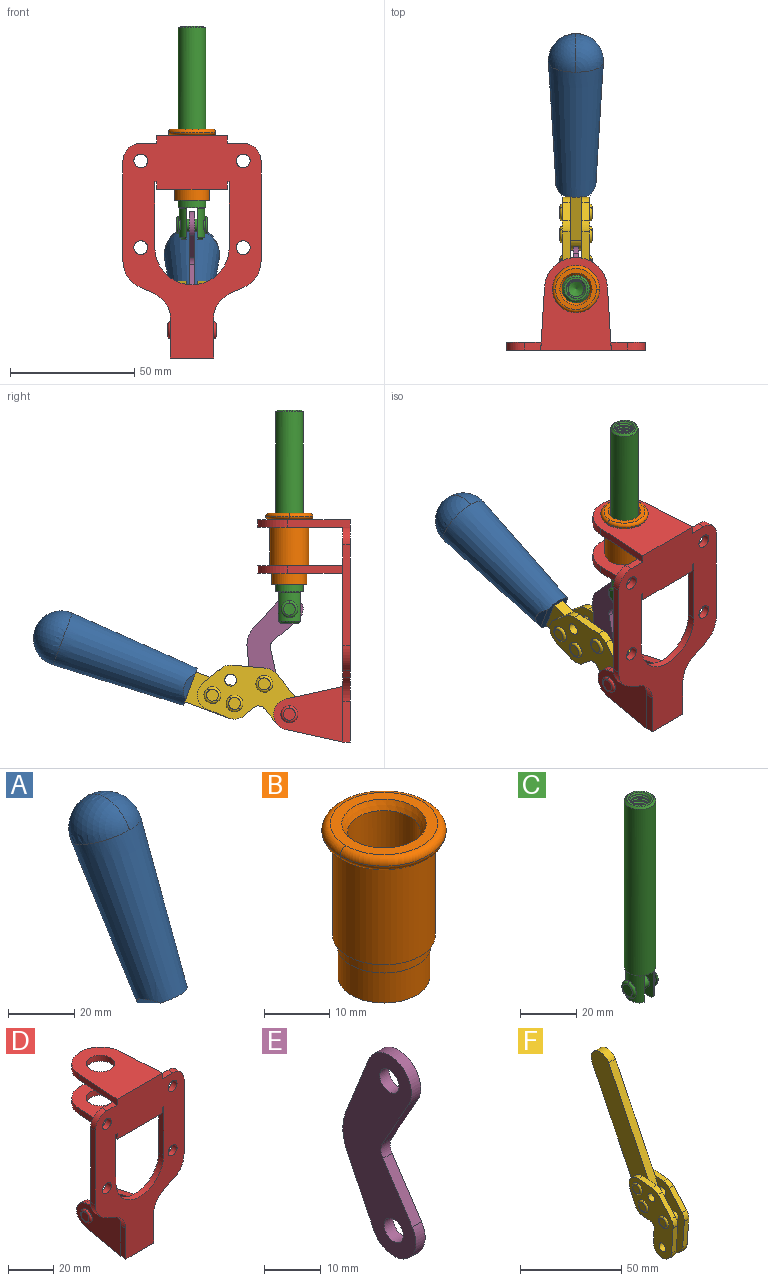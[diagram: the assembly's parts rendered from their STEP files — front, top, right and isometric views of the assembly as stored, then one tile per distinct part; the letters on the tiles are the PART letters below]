
ASSEMBLY  parts=6 mates=6
PART A: 11 faces, bbox 22.3x42.6x64.5 mm
  f0: sphere r=11.13mm, area 411.4mm2, adj f1,f8
  f1: cone r=11.11mm half-angle=3.3deg, axis (0,0.44,0.9), area 3251.8mm2, adj f0,f7,f8,f9,f10
  f2: cylinder r=6.16mm len=11.7mm, axis (1,0,0), area 89.5mm2, adj f3,f4,f5,f6
  f3: plane 60.23x36.75mm, normal (-1,0,0), area 763.6mm2, adj f2,f4,f6,f10
  f4: plane 51.37x25.05mm, normal (0,0.9,-0.44), area 264.2mm2, adj f2,f3,f5,f10
  f5: plane 60.23x36.75mm, normal (1,0,0), area 763.6mm2, adj f2,f4,f6,f10
  f6: plane 51.37x25.05mm, normal (0,-0.9,0.44), area 264.2mm2, adj f2,f3,f5,f10
  f7: plane 9.95x5.95mm, normal (0.71,-0.31,-0.64), area 25.8mm2, adj f1,f10
  f8: sphere r=11.13mm, area 411.4mm2, adj f0,f1
  f9: plane 9.95x5.95mm, normal (-0.71,-0.31,-0.64), area 25.8mm2, adj f1,f10
  f10: plane 14.27x11.38mm, normal (0,-0.44,-0.9), area 106.7mm2, adj f1,f3,f4,f5,f6,f7,f9
PART B: 15 faces, bbox 20.6x20.6x28.7 mm
  f0: torus R=8.26mm, axis (0,0,1), area 56.8mm2, adj f1,f10,f12
  f1: torus R=8.26mm, axis (0,0,1), area 56.8mm2, adj f0,f6,f13
  f2: cylinder r=5.59mm len=25.91mm, axis (0,0,1), area 909.6mm2, adj f3,f4
  f3: cone r=6.86mm half-angle=45deg, axis (0,0,-1), area 70.2mm2, adj f2,f14
  f4: cone r=6.47mm half-angle=30deg, axis (0,0,1), area 66.7mm2, adj f2,f13
  f5: cylinder r=7.04mm len=14.07mm, axis (0,0,1), area 252.6mm2, adj f11,f14
  f6: torus R=8.26mm, axis (0,0,1), area 56.8mm2, adj f1,f12,f13
  f7: cylinder r=7.16mm len=14.33mm, axis (0,0,1), area 91.5mm2, adj f9,f11
  f8: cylinder r=7.86mm len=18.42mm, axis (0,0,1), area 909.6mm2, adj f9,f10
  f9: plane 15.72x15.72mm, normal (0,0,-1), area 33mm2, adj f7,f8
  f10: plane 16.51x16.51mm, normal (0,0,-1), area 19.9mm2, adj f0,f8,f12
  f11: plane 14.33x14.33mm, normal (0,0,-1), area 5.7mm2, adj f5,f7
  f12: torus R=8.26mm, axis (0,0,1), area 56.8mm2, adj f0,f6,f10
  f13: plane 16.51x16.51mm, normal (0,0,1), area 82.7mm2, adj f1,f4,f6
  f14: plane 14.07x14.07mm, normal (0,0,-1), area 7.8mm2, adj f3,f5
PART C: 48 faces, bbox 12.6x11.1x86.1 mm
  f0: torus R=2.41mm, axis (-1,0,0), area 15mm2, adj f30,f32,f34
  f1: torus R=2.41mm, axis (-1,0,0), area 15mm2, adj f29,f31,f33
  f2: cylinder r=5.54mm len=72.39mm, axis (0,0,1), area 2518.5mm2, adj f3,f4,f42,f43
  f3: cone r=5.54mm half-angle=45deg, axis (0,0,1), area 7.6mm2, adj f2,f5,f41
  f4: cone r=5.54mm half-angle=45deg, axis (0,0,-1), area 34.9mm2, adj f2,f39
  f5: cylinder r=5.08mm len=11.48mm, axis (0,0,1), area 108.3mm2, adj f3,f7,f8,f41
  f6: cylinder r=2.41mm len=4.83mm, axis (-1,0,0), area 71.2mm2, adj f40,f41
  f7: cylinder r=2.41mm len=4.83mm, axis (-1,0,0), area 7.6mm2, adj f5,f34
  f8: cone r=5.08mm half-angle=45deg, axis (0,0,1), area 10.6mm2, adj f5,f37,f41
  f9: cone r=3.98mm half-angle=45deg, axis (0,0,1), area 17.6mm2, adj f27,f39,f45,f46,f47
  f10: cylinder r=2.41mm len=4.83mm, axis (-1,0,0), area 7.6mm2, adj f33,f38
  f11: cylinder r=3.2mm len=6.4mm, axis (0,0,1), area 78.4mm2, adj f12,f28,f44,f45,f47
  f12: cylinder r=3.2mm len=6.4mm, axis (0,0,1), area 10.5mm2, adj f11,f13,f45,f47
  f13: cylinder r=3.2mm len=6.4mm, axis (0,0,1), area 10.5mm2, adj f12,f14,f45,f47
  f14: cylinder r=3.2mm len=6.4mm, axis (0,0,1), area 10.5mm2, adj f13,f15,f45,f47
  f15: cylinder r=3.2mm len=6.4mm, axis (0,0,1), area 10.5mm2, adj f14,f16,f45,f47
  f16: cylinder r=3.2mm len=6.4mm, axis (0,0,1), area 10.5mm2, adj f15,f17,f45,f47
  f17: cylinder r=3.2mm len=6.4mm, axis (0,0,1), area 10.5mm2, adj f16,f18,f45,f47
  f18: cylinder r=3.2mm len=6.4mm, axis (0,0,1), area 10.5mm2, adj f17,f19,f45,f47
  f19: cylinder r=3.2mm len=6.4mm, axis (0,0,1), area 10.5mm2, adj f18,f20,f45,f47
  f20: cylinder r=3.2mm len=6.4mm, axis (0,0,1), area 10.5mm2, adj f19,f21,f45,f47
  f21: cylinder r=3.2mm len=6.4mm, axis (0,0,1), area 10.5mm2, adj f20,f22,f45,f47
  f22: cylinder r=3.2mm len=6.4mm, axis (0,0,1), area 10.5mm2, adj f21,f23,f45,f47
  f23: cylinder r=3.2mm len=6.4mm, axis (0,0,1), area 10.5mm2, adj f22,f24,f45,f47
  f24: cylinder r=3.2mm len=6.4mm, axis (0,0,1), area 10.5mm2, adj f23,f25,f45,f47
  f25: cylinder r=3.2mm len=6.4mm, axis (0,0,1), area 10.5mm2, adj f24,f26,f45,f47
  f26: cylinder r=3.2mm len=6.4mm, axis (0,0,1), area 10.5mm2, adj f25,f27,f45,f47
  f27: cylinder r=3.2mm len=6.4mm, axis (0,0,1), area 7.4mm2, adj f9,f26,f45,f47
  f28: cone r=3.2mm half-angle=60deg, axis (0,0,1), area 37.2mm2, adj f11
  f29: plane 4.83x4.83mm, normal (-1,0,0), area 18.3mm2, adj f1,f31
  f30: plane 4.83x4.83mm, normal (1,0,0), area 18.3mm2, adj f0,f32
  f31: torus R=2.41mm, axis (-1,0,0), area 15mm2, adj f1,f29,f33
  f32: torus R=2.41mm, axis (-1,0,0), area 15mm2, adj f0,f30,f34
  f33: plane 6.83x6.83mm, normal (1,0,0), area 18.3mm2, adj f1,f10,f31
  f34: plane 6.83x6.83mm, normal (-1,0,0), area 18.3mm2, adj f0,f7,f32
  f35: cone r=5.08mm half-angle=45deg, axis (0,0,1), area 10.6mm2, adj f36,f38,f40
  f36: plane 7.25x1.97mm, normal (0,0,-1), area 10mm2, adj f35,f40
  f37: plane 7.25x1.97mm, normal (0,0,-1), area 10mm2, adj f8,f41
  f38: cylinder r=5.08mm len=11.48mm, axis (0,0,1), area 108.3mm2, adj f10,f35,f40,f42
  f39: plane 9.55x9.55mm, normal (0,0,1), area 22mm2, adj f4,f9
  f40: plane 12.76x10.09mm, normal (1,0,0), area 95.7mm2, adj f6,f35,f36,f38,f42,f43
  f41: plane 12.76x10.09mm, normal (-1,0,0), area 95.7mm2, adj f3,f5,f6,f8,f37,f43
  f42: cone r=5.54mm half-angle=45deg, axis (0,0,1), area 7.6mm2, adj f2,f38,f40
  f43: plane 11.07x4.7mm, normal (0,0,-1), area 50.4mm2, adj f2,f40,f41
  f44: plane 0.89x0.62mm, normal (-1,0,0), area 0.3mm2, adj f11,f45,f46,f47
  f45: bspline ~24.8x7.63mm, area 266.6mm2, adj f9,f11,f12,f13,f14,f15,f16,f17
  f46: bspline ~24.87x7.63mm, area 73.6mm2, adj f9,f44,f45,f47
  f47: bspline ~24.98x7.63mm, area 272.5mm2, adj f9,f11,f12,f13,f14,f15,f16,f17
PART D: 55 faces, bbox 55.7x37.4x89.8 mm
  f0: torus R=2.41mm, axis (-1,0,0), area 15mm2, adj f11,f15,f25
  f1: torus R=2.41mm, axis (-1,0,0), area 15mm2, adj f10,f12,f22
  f2: cylinder r=2.78mm len=5.56mm, axis (0,-1,0), area 54.2mm2, adj f30,f54
  f3: cylinder r=14.99mm len=29.97mm, axis (0,-1,0), area 145.9mm2, adj f30,f49,f53,f54
  f4: cylinder r=2.78mm len=5.56mm, axis (0,-1,0), area 54.2mm2, adj f30,f54
  f5: cylinder r=2.78mm len=5.56mm, axis (0,-1,0), area 54.2mm2, adj f30,f54
  f6: cylinder r=2.78mm len=5.56mm, axis (0,-1,0), area 54.2mm2, adj f30,f54
  f7: cylinder r=6.35mm len=12.7mm, axis (0,0,1), area 123.6mm2, adj f27,f51
  f8: cylinder r=6.35mm len=12.7mm, axis (0,0,-1), area 124.7mm2, adj f21,f35
  f9: cylinder r=2.41mm len=11.18mm, axis (-1,0,0), area 169.4mm2, adj f16,f19
  f10: plane 4.83x4.83mm, normal (1,0,0), area 18.3mm2, adj f1,f12
  f11: plane 4.83x4.83mm, normal (-1,0,0), area 18.3mm2, adj f0,f15
  f12: torus R=2.41mm, axis (-1,0,0), area 15mm2, adj f1,f10,f22
  f13: cylinder r=6.35mm len=12.41mm, axis (1,0,0), area 53.4mm2, adj f18,f19,f22,f23
  f14: cylinder r=6.35mm len=12.41mm, axis (-1,0,0), area 53.4mm2, adj f16,f17,f24,f25
  f15: torus R=2.41mm, axis (-1,0,0), area 15mm2, adj f0,f11,f25
  f16: plane 27.86x22.35mm, normal (1,0,0), area 425.4mm2, adj f9,f14,f17,f24,f30
  f17: plane 22.86x4.97mm, normal (0,0.21,0.98), area 72.5mm2, adj f14,f16,f25,f30
  f18: plane 22.86x4.97mm, normal (0,0.21,0.98), area 72.5mm2, adj f13,f19,f22,f30
  f19: plane 27.86x22.35mm, normal (-1,0,0), area 425.4mm2, adj f9,f13,f18,f23,f30
  f20: cylinder r=12.7mm len=25.35mm, axis (0,0,-1), area 119.8mm2, adj f21,f34,f35,f36
  f21: plane 34.21x28.07mm, normal (0,0,-1), area 702.4mm2, adj f8,f20,f30,f34,f36
  f22: plane 27.96x22.45mm, normal (1,0,0), area 407.2mm2, adj f1,f12,f13,f18,f23,f30,f42,f43
  f23: plane 22.86x4.97mm, normal (0,0.21,-0.98), area 72.5mm2, adj f13,f19,f22,f44
  f24: plane 22.86x4.97mm, normal (0,0.21,-0.98), area 72.5mm2, adj f14,f16,f25,f44
  f25: plane 27.86x22.35mm, normal (-1,0,0), area 407.1mm2, adj f0,f14,f15,f17,f24,f30,f45,f46
  f26: plane 3.1x0.95mm, normal (0,0,-1), area 2.7mm2, adj f30,f49,f50,f54
  f27: plane 34.21x28.07mm, normal (0,0,1), area 702.4mm2, adj f7,f28,f30,f50,f52
  f28: cylinder r=12.7mm len=25.35mm, axis (0,0,1), area 118.8mm2, adj f27,f50,f51,f52
  f29: plane 3.1x0.95mm, normal (0,0,-1), area 2.7mm2, adj f30,f52,f53,f54
  f30: plane 86.54x55.63mm, normal (0,1,0), area 2362.9mm2, adj f2,f3,f4,f5,f6,f16,f17,f18
  f31: plane 40.56x3.1mm, normal (-1,0,0), area 125.7mm2, adj f30,f32,f48,f54
  f32: cylinder r=7.11mm len=7.11mm, axis (0,-1,0), area 34.6mm2, adj f30,f31,f33,f54
  f33: plane 6.67x3.1mm, normal (0,0,1), area 20.4mm2, adj f30,f32,f34,f54
  f34: plane 25.39x3.13mm, normal (-1,0.06,0), area 79.5mm2, adj f20,f21,f33,f35,f54
  f35: plane 37.31x28.45mm, normal (0,0,1), area 789.9mm2, adj f8,f20,f34,f36,f54
  f36: plane 25.39x3.13mm, normal (1,0.06,0), area 79.5mm2, adj f20,f21,f35,f37,f54
  f37: plane 6.67x3.1mm, normal (0,0,1), area 20.4mm2, adj f30,f36,f38,f54
  f38: cylinder r=7.11mm len=7.11mm, axis (0,-1,0), area 34.6mm2, adj f30,f37,f39,f54
  f39: plane 40.56x3.1mm, normal (1,0,0), area 125.7mm2, adj f30,f38,f40,f54
  f40: cylinder r=11.18mm len=10.16mm, axis (0,-1,0), area 39.5mm2, adj f30,f39,f41,f54
  f41: plane 6.09x3.1mm, normal (0.42,0,-0.91), area 20.8mm2, adj f30,f40,f42,f54
  f42: cylinder r=11.18mm len=9.41mm, axis (0,-1,0), area 37.2mm2, adj f22,f30,f41,f43,f54
  f43: plane 16.5x3.1mm, normal (1,0,0), area 51.1mm2, adj f22,f42,f44,f54
  f44: plane 17.37x3.1mm, normal (0,0,-1), area 53.8mm2, adj f23,f24,f30,f43,f45,f54
  f45: plane 16.5x3.1mm, normal (-1,0,0), area 51.1mm2, adj f25,f44,f46,f54
  f46: cylinder r=11.18mm len=9.41mm, axis (0,-1,0), area 37.2mm2, adj f25,f30,f45,f47,f54
  f47: plane 6.09x3.1mm, normal (-0.42,0,-0.91), area 20.8mm2, adj f30,f46,f48,f54
  f48: cylinder r=11.18mm len=10.16mm, axis (0,-1,0), area 39.5mm2, adj f30,f31,f47,f54
  f49: plane 26.54x3.1mm, normal (-1,0,0), area 82.3mm2, adj f3,f26,f30,f54
  f50: plane 25.39x3.1mm, normal (1,0.06,0), area 78.8mm2, adj f26,f27,f28,f51,f54
  f51: plane 37.31x28.45mm, normal (0,0,-1), area 789.9mm2, adj f7,f28,f50,f52,f54
  f52: plane 25.39x3.1mm, normal (-1,0.06,0), area 78.8mm2, adj f27,f28,f29,f51,f54
  f53: plane 26.54x3.1mm, normal (1,0,0), area 82.3mm2, adj f3,f29,f30,f54
  f54: plane 89.66x55.63mm, normal (0,-1,0), area 2678.5mm2, adj f2,f3,f4,f5,f6,f26,f29,f31
PART E: 12 faces, bbox 2.3x18.2x42.8 mm
  f0: cylinder r=2.4mm len=4.8mm, axis (1,0,0), area 34.9mm2, adj f4,f11
  f1: cylinder r=10.41mm len=8.47mm, axis (1,0,0), area 20.2mm2, adj f4,f9,f10,f11
  f2: cylinder r=3.05mm len=3.16mm, axis (1,0,0), area 7.7mm2, adj f4,f6,f7,f11
  f3: cylinder r=2.4mm len=4.8mm, axis (1,0,0), area 34.9mm2, adj f4,f11
  f4: plane 42.81x18.23mm, normal (-1,0,0), area 414.1mm2, adj f0,f1,f2,f3,f5,f6,f7,f8
  f5: cylinder r=5.54mm len=10.67mm, axis (1,0,0), area 41.8mm2, adj f4,f6,f10,f11
  f6: plane 11.66x6.53mm, normal (0,-0.87,-0.49), area 30.9mm2, adj f2,f4,f5,f11
  f7: plane 11.17x7.33mm, normal (0,-0.84,0.55), area 30.9mm2, adj f2,f4,f8,f11
  f8: cylinder r=5.54mm len=10.51mm, axis (1,0,0), area 41.8mm2, adj f4,f7,f9,f11
  f9: plane 13.67x6.67mm, normal (0,0.9,-0.44), area 35.1mm2, adj f1,f4,f8,f11
  f10: plane 14.1x5.7mm, normal (0,0.93,0.37), area 35.1mm2, adj f1,f4,f5,f11
  f11: plane 42.81x18.23mm, normal (1,0,0), area 414.1mm2, adj f0,f1,f2,f3,f5,f6,f7,f8
PART F: 59 faces, bbox 12.9x60.2x99.6 mm
  f0: torus R=2.39mm, axis (-1,0,0), area 14.9mm2, adj f20,f43,f51
  f1: torus R=2.39mm, axis (-1,0,0), area 14.9mm2, adj f19,f42,f51
  f2: torus R=2.39mm, axis (-1,0,0), area 14.9mm2, adj f18,f35,f51
  f3: torus R=2.39mm, axis (-1,0,0), area 14.9mm2, adj f14,f17,f23
  f4: torus R=2.39mm, axis (-1,0,0), area 14.9mm2, adj f13,f16,f23
  f5: torus R=2.39mm, axis (-1,0,0), area 14.9mm2, adj f12,f15,f23
  f6: cylinder r=2.39mm len=4.78mm, axis (1,0,0), area 46.5mm2, adj f48,f50,f51
  f7: cylinder r=2.39mm len=4.78mm, axis (1,0,0), area 46.5mm2, adj f50,f51
  f8: cylinder r=6.35mm len=12.68mm, axis (1,0,0), area 61.8mm2, adj f38,f39,f50,f51
  f9: cylinder r=2.39mm len=4.78mm, axis (-1,0,0), area 70.5mm2, adj f46,f50
  f10: cylinder r=2.39mm len=4.78mm, axis (-1,0,0), area 46.5mm2, adj f23,f45,f46
  f11: cylinder r=2.39mm len=4.78mm, axis (-1,0,0), area 46.5mm2, adj f23,f46
  f12: plane 4.78x4.78mm, normal (1,0,0), area 17.9mm2, adj f5,f15
  f13: plane 4.78x4.78mm, normal (1,0,0), area 17.9mm2, adj f4,f16
  f14: plane 4.78x4.78mm, normal (1,0,0), area 17.9mm2, adj f3,f17
  f15: torus R=2.39mm, axis (-1,0,0), area 14.9mm2, adj f5,f12,f23
  f16: torus R=2.39mm, axis (-1,0,0), area 14.9mm2, adj f4,f13,f23
  f17: torus R=2.39mm, axis (-1,0,0), area 14.9mm2, adj f3,f14,f23
  f18: plane 4.78x4.78mm, normal (-1,0,0), area 17.9mm2, adj f2,f35
  f19: plane 4.78x4.78mm, normal (-1,0,0), area 17.9mm2, adj f1,f42
  f20: plane 4.78x4.78mm, normal (-1,0,0), area 17.9mm2, adj f0,f43
  f21: plane 2.26x0.2mm, normal (1,0,0), area 0.2mm2, adj f31,f44
  f22: plane 2.26x0.2mm, normal (-1,0,0), area 0.2mm2, adj f41,f44
  f23: plane 39.37x30.77mm, normal (1,0,0), area 565.5mm2, adj f3,f4,f5,f10,f11,f15,f16,f17
  f24: cylinder r=6.1mm len=4.15mm, axis (-1,0,0), area 14.7mm2, adj f23,f25,f32,f46
  f25: plane 10.25x9.01mm, normal (0,-0.75,0.66), area 42.3mm2, adj f23,f24,f26,f46
  f26: cylinder r=6.35mm len=4.64mm, axis (-1,0,0), area 15.6mm2, adj f23,f25,f27,f46
  f27: plane 15.84x3.1mm, normal (0,-1,-0.07), area 49.2mm2, adj f23,f26,f28,f46
  f28: cylinder r=6.35mm len=12.68mm, axis (-1,0,0), area 61.8mm2, adj f23,f27,f29,f46
  f29: plane 8.11x3.1mm, normal (0,1,0.07), area 25.2mm2, adj f23,f28,f30,f46
  f30: cylinder r=3.05mm len=3.25mm, axis (-1,0,0), area 14.8mm2, adj f23,f29,f31,f46
  f31: plane 5.99x3.1mm, normal (0,0.07,-1), area 18.6mm2, adj f21,f23,f30,f44,f46
  f32: plane 9.5x3.1mm, normal (0,-0.07,1), area 29.5mm2, adj f23,f24,f33,f46,f47
  f33: cylinder r=6.1mm len=8.63mm, axis (-1,0,0), area 39.1mm2, adj f23,f32,f34,f47
  f34: plane 8.65x3.96mm, normal (0,0.91,-0.42), area 29.5mm2, adj f23,f33,f44,f47
  f35: torus R=2.39mm, axis (-1,0,0), area 14.9mm2, adj f2,f18,f51
  f36: plane 10.25x9.01mm, normal (0,-0.75,0.66), area 42.3mm2, adj f37,f49,f50,f51
  f37: cylinder r=6.35mm len=4.64mm, axis (1,0,0), area 15.6mm2, adj f36,f38,f50,f51
  f38: plane 15.84x3.1mm, normal (0,-1,-0.07), area 49.2mm2, adj f8,f37,f50,f51
  f39: plane 8.11x3.1mm, normal (0,1,0.07), area 25.2mm2, adj f8,f40,f50,f51
  f40: cylinder r=3.05mm len=3.25mm, axis (1,0,0), area 14.8mm2, adj f39,f41,f50,f51
  f41: plane 5.99x3.1mm, normal (0,0.07,-1), area 18.6mm2, adj f22,f40,f44,f50,f51
  f42: torus R=2.39mm, axis (-1,0,0), area 14.9mm2, adj f1,f19,f51
  f43: torus R=2.39mm, axis (-1,0,0), area 14.9mm2, adj f0,f20,f51
  f44: cylinder r=6.35mm len=12.12mm, axis (-1,0,0), area 128.9mm2, adj f21,f22,f23,f31,f34,f41,f46,f47
  f45: plane 2.65x1.35mm, normal (1,0,0), area 1mm2, adj f10,f55
  f46: plane 39.08x20.42mm, normal (-1,0,0), area 412.5mm2, adj f9,f10,f11,f24,f25,f26,f27,f28
  f47: plane 77.62x39.82mm, normal (1,0,0), area 850mm2, adj f32,f33,f34,f44,f53,f54,f55
  f48: plane 2.65x1.35mm, normal (-1,0,0), area 1mm2, adj f6,f55
  f49: cylinder r=6.1mm len=4.15mm, axis (1,0,0), area 14.7mm2, adj f36,f50,f51,f56
  f50: plane 39.08x20.42mm, normal (1,0,0), area 412.5mm2, adj f6,f7,f8,f9,f36,f37,f38,f39
  f51: plane 39.37x30.77mm, normal (-1,0,0), area 565.5mm2, adj f0,f1,f2,f6,f7,f8,f35,f36
  f52: plane 8.65x3.96mm, normal (0,0.91,-0.42), area 29.5mm2, adj f44,f51,f57,f58
  f53: plane 68.49x33.4mm, normal (0,0.9,-0.44), area 358.1mm2, adj f44,f47,f54,f58
  f54: cylinder r=6.35mm len=12.06mm, axis (1,0,0), area 93.7mm2, adj f47,f53,f55,f58
  f55: plane 68.49x33.4mm, normal (0,-0.9,0.44), area 358.1mm2, adj f44,f45,f46,f47,f48,f50,f54,f58
  f56: plane 9.5x3.1mm, normal (0,-0.07,1), area 29.5mm2, adj f49,f50,f51,f57,f58
  f57: cylinder r=6.1mm len=8.63mm, axis (1,0,0), area 39.1mm2, adj f51,f52,f56,f58
  f58: plane 77.62x39.82mm, normal (-1,0,0), area 850mm2, adj f44,f52,f53,f54,f55,f56,f57
PLACE A rot(axis=(-1,0,0),43.5deg) t=(-0.24,24.16,8.13)mm
PLACE B t=(-0.2,-4.67,0)mm
PLACE C t=(-0.2,-4.67,-5.21)mm
PLACE D t=(-0.2,-4.67,0)mm fixed
PLACE E rot(axis=(1,0,0),20.5deg) t=(-0.2,2.32,-12.86)mm
PLACE F rot(axis=(-1,0,0),43.5deg) t=(-0.2,24.16,8.13)mm
MATE revolute E.f5 <-> C.f1  axis (1,0,0) through (-0.2,19.94,10.27)mm
MATE revolute D.f0 <-> F.f7  axis (-1,0,0) through (-0.2,19.94,-32.09)mm
MATE revolute F.f4 <-> E.f3  axis (-1,0,0) through (-0.2,30.04,-19.84)mm
MATE fastened B.f0 <-> D.f7  axis (0,0,-1) through (-0.2,19.94,46.39)mm
MATE fastened A.f2 <-> F.f54  axis (1,0,0) through (-2.55,113.4,-0.99)mm
MATE slider C.f2 <-> D.f7  axis (0,0,1) through (-0.2,19.94,53.57)mm
